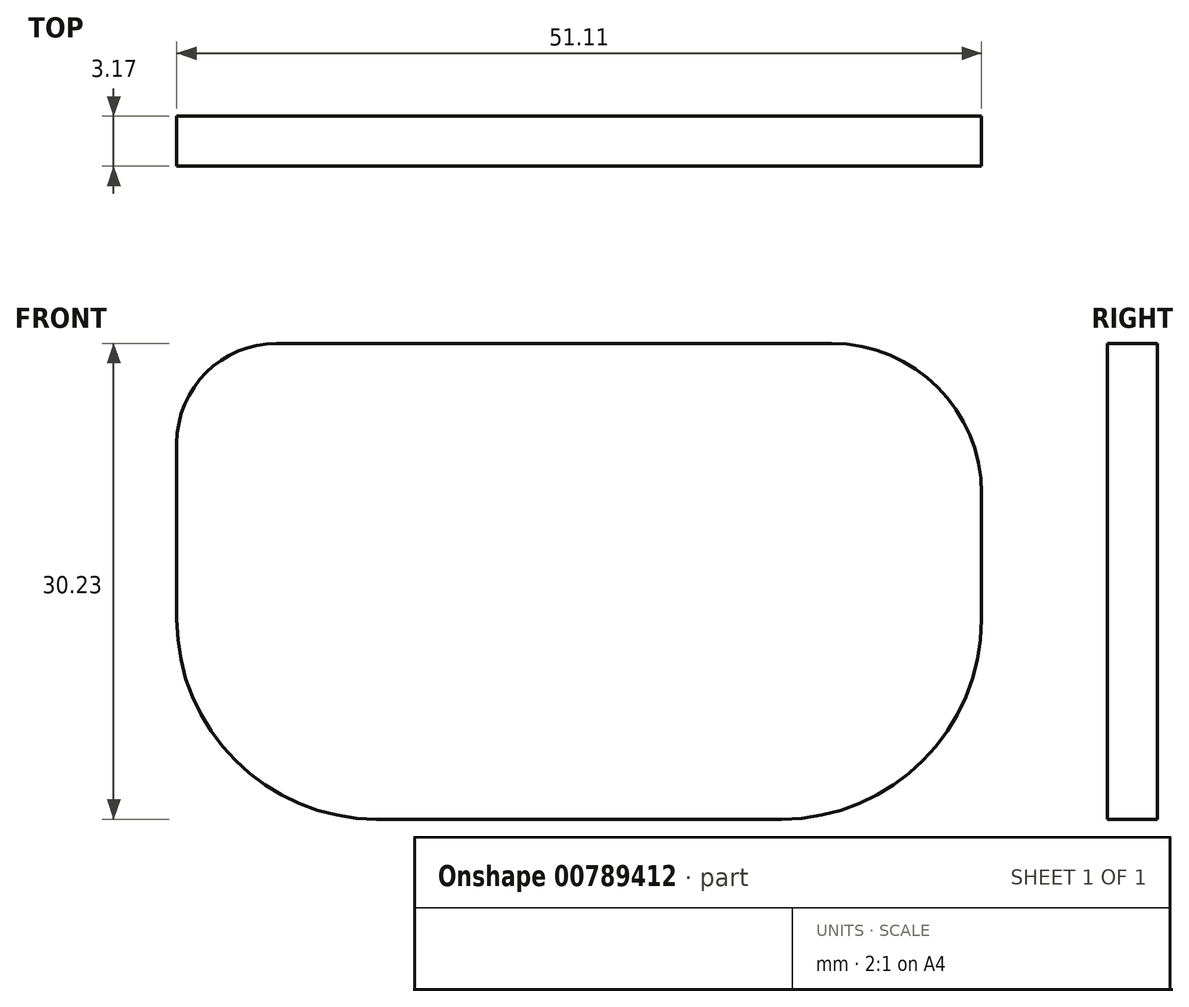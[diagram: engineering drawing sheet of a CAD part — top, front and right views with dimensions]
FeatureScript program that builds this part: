
annotation { "Feature Type Name" : "Feature", "Feature Type Description" : "" }
export const myFeature = defineFeature(function(context is Context, id is Id, definition is map)
    precondition{}
    {
        {
            var Q0;
            Q0=qCreatedBy(makeId("Front.planeOp"),FACE);
            var sketch = newSketch(context, id + "F0", { "sketchPlane" : qUnion([Q0])});
            skLineSegment(sketch, "E0.bottom", {"start": v(-53.7, 46.37) * mm, "end": v(-18.46, 46.37) * mm});
            skLineSegment(sketch, "E0.top", {"start": v(-47.35, 16.14) * mm, "end": v(-21.64, 16.14) * mm});
            skLineSegment(sketch, "E0.left", {"start": v(-60.05, 40.02) * mm, "end": v(-60.05, 28.84) * mm});
            skLineSegment(sketch, "E0.right", {"start": v(-8.94, 36.84) * mm, "end": v(-8.94, 28.84) * mm});
            skPoint(sketch, "E1.visualSharp", {"position": v(-60.05, 46.37) * mm});
            skArc(sketch, "E1.filletArc", {"start": v(-53.7, 46.37) * mm, "mid": v(-58.19, 44.5) * mm, "end": v(-60.05, 40.02) * mm});
            skPoint(sketch, "E2.visualSharp", {"position": v(-60.05, 16.14) * mm});
            skArc(sketch, "E2.filletArc", {"start": v(-60.05, 28.84) * mm, "mid": v(-56.33, 19.86) * mm, "end": v(-47.35, 16.14) * mm});
            skPoint(sketch, "E3.visualSharp", {"position": v(-8.94, 46.37) * mm});
            skArc(sketch, "E3.filletArc", {"start": v(-8.94, 36.84) * mm, "mid": v(-11.73, 43.58) * mm, "end": v(-18.46, 46.37) * mm});
            skPoint(sketch, "E4.visualSharp", {"position": v(-8.94, 16.14) * mm});
            skArc(sketch, "E4.filletArc", {"start": v(-21.64, 16.14) * mm, "mid": v(-12.66, 19.86) * mm, "end": v(-8.94, 28.84) * mm});
            skSolve(sketch);
        }
        {
            var Q0;
            Q0 = qSketchRegion(id + "F0", true);
            extrude(context, id + "F1", {"entities" : qUnion([Q0]), "depth" : 3.17 * mm, "offsetDistance" : 25.4 * mm});
        }
    });
